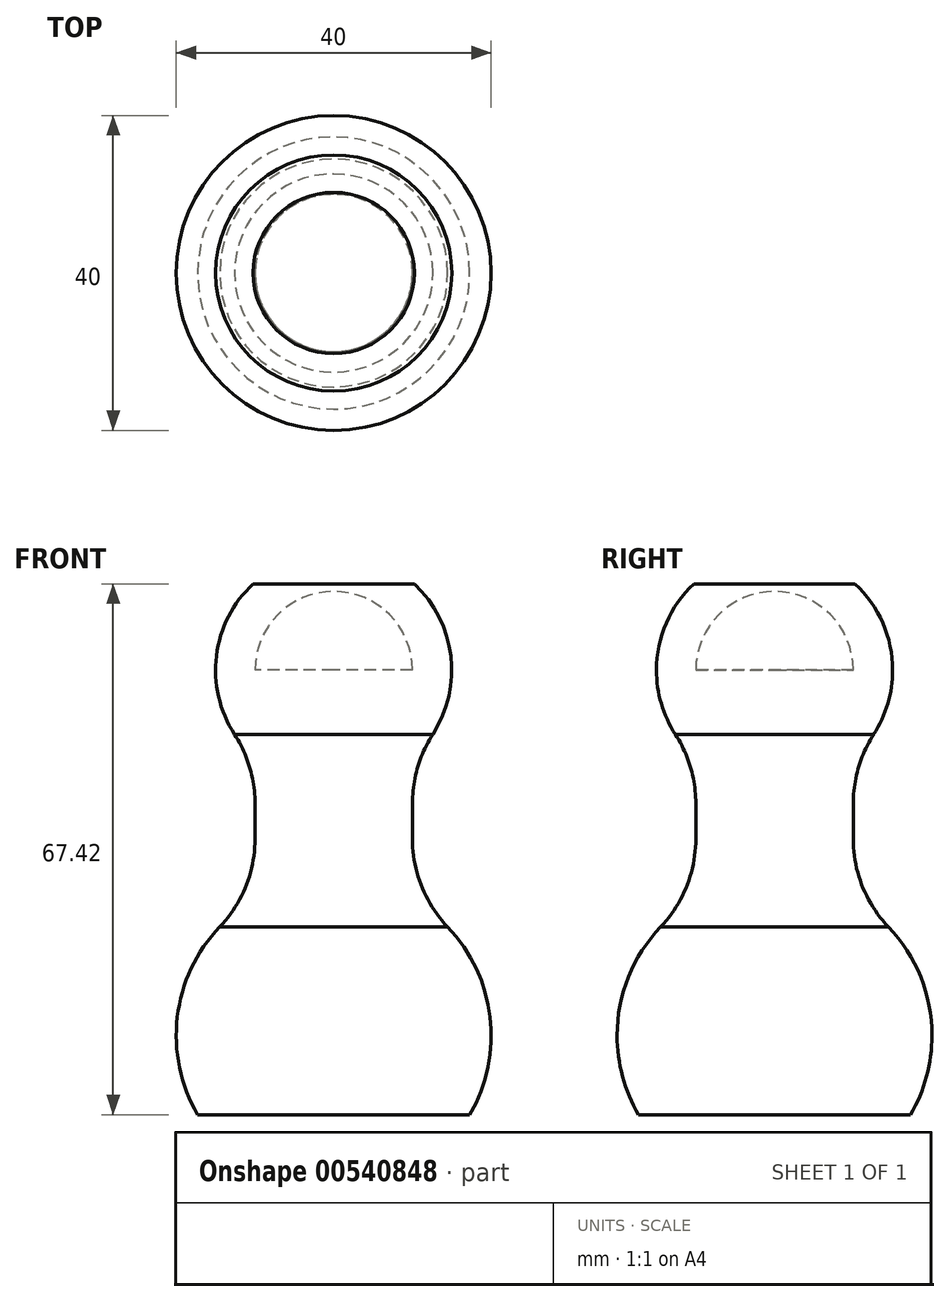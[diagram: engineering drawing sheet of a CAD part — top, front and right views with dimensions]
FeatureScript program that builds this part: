
annotation { "Feature Type Name" : "Feature", "Feature Type Description" : "" }
export const myFeature = defineFeature(function(context is Context, id is Id, definition is map)
    precondition{}
    {
        {
            var Q0;
            Q0=qCreatedBy(makeId("Top.planeOp"),FACE);
            var sketch = newSketch(context, id + "F0", { "sketchPlane" : qUnion([Q0])});
            skArc(sketch, "E0", {"start": v(0, 20) * mm, "mid": v(-20, 0) * mm, "end": v(0, -20) * mm});
            skLineSegment(sketch, "E1", {"start": v(0, 20) * mm, "end": v(0, -20) * mm});
            skSolve(sketch);
        }
        {
            var Q0;
            Q0=makeQuery(id+"F0.imprint","IMPRINT",FACE,{"disambiguationData":[TD([[makeQuery(id+"F0.imprint","IMPRINT",EDGE,{"derivedFrom":sQuery(id+"F0.wireOp",EDGE,"E0")}),1.0]])]});
            var Q1;
            Q1=sQuery(id+"F0.wireOp",EDGE,"E1");
            revolve(context, id + "F1", {"entities" : qUnion([Q0]), "axis" : qUnion([Q1]), "revolveType" : RevolveType.FULL});
        }
        {
            var Q0;
            Q0=qCreatedBy(makeId("Top.planeOp"),FACE);
            var sketch = newSketch(context, id + "F2", { "sketchPlane" : qUnion([Q0])});
            skCircle(sketch, "E2", {"center": v(0, 0) * mm, "radius": 10 * mm});
            skSolve(sketch);
        }
        {
            var Q0;
            Q0 = qSketchRegion(id + "F2", true);
            extrude(context, id + "F3", {"entities" : qUnion([Q0]), "operationType" : NewBodyOperationType.ADD, "depth" : 46.4 * mm, "offsetDistance" : 25 * mm});
        }
        {
            var Q0;
            Q0=makeQuery(id+"F3.opExtrude","CAP_FACE",FACE,{"disambiguationData":[OSD([sQuery(id+"F2.wireOp",EDGE,"E2")])],"isStart":false});
            var sketch = newSketch(context, id + "F4", { "sketchPlane" : qUnion([Q0])});
            skArc(sketch, "E3", {"start": v(0, 15) * mm, "mid": v(-15, 0) * mm, "end": v(0, -15) * mm});
            skLineSegment(sketch, "E4", {"start": v(0, 15) * mm, "end": v(0, -15) * mm});
            skSolve(sketch);
        }
        {
            var Q0;
            Q0=makeQuery(id+"F4.imprint","IMPRINT",FACE,{"disambiguationData":[TD([[makeQuery(id+"F4.imprint","IMPRINT",EDGE,{"derivedFrom":sQuery(id+"F4.wireOp",EDGE,"E3")}),1.0]])]});
            var Q1;
            Q1=sQuery(id+"F4.wireOp",EDGE,"E4");
            revolve(context, id + "F5", {"operationType" : NewBodyOperationType.ADD, "entities" : qUnion([Q0]), "axis" : qUnion([Q1]), "revolveType" : RevolveType.FULL});
        }
        {
            var Q0;
            Q0=makeQuery(id+"F5.boolean.opBoolean","INTERSECT",EDGE,{"derivedFrom":[makeQuery(id+"F3.opExtrude","SWEPT_FACE",FACE,{"disambiguationData":[OSD([sQuery(id+"F2.wireOp",EDGE,"E2")])]}),makeQuery(id+"F5.opRevolve","SWEPT_FACE",FACE,{"disambiguationData":[OSD([sQuery(id+"F4.wireOp",EDGE,"E3")])]})]});
            var Q1;
            Q1=makeQuery(id+"F3.boolean.opBoolean","INTERSECT",EDGE,{"derivedFrom":[makeQuery(id+"F1.opRevolve","SWEPT_FACE",FACE,{"disambiguationData":[OSD([sQuery(id+"F0.wireOp",EDGE,"E0")])]}),makeQuery(id+"F3.opExtrude","SWEPT_FACE",FACE,{"disambiguationData":[OSD([sQuery(id+"F2.wireOp",EDGE,"E2")])]})]});
            fillet(context, id + "F6", {"entities" : qUnion([Q0, Q1]), "radius" : 16.16 * mm, "tangentPropagation" : true, "allowEdgeOverflow" : false});
        }
        {
            var Q0;
            Q0=qCreatedBy(makeId("Front.planeOp"),FACE);
            var sketch = newSketch(context, id + "F7", { "sketchPlane" : qUnion([Q0])});
            skLineSegment(sketch, "E5.bottom", {"start": v(-35.85, 57.36) * mm, "end": v(40.38, 57.36) * mm});
            skLineSegment(sketch, "E5.top", {"start": v(-35.85, -10.06) * mm, "end": v(40.38, -10.06) * mm});
            skLineSegment(sketch, "E5.left", {"start": v(-35.85, 57.36) * mm, "end": v(-35.85, -10.06) * mm});
            skLineSegment(sketch, "E5.right", {"start": v(40.38, 57.36) * mm, "end": v(40.38, -10.06) * mm});
            skSolve(sketch);
        }
        {
            var Q0;
            Q0=makeQuery(id+"F7.imprint","IMPRINT",FACE,{"disambiguationData":[TD([[makeQuery(id+"F7.imprint","IMPRINT",EDGE,{"derivedFrom":sQuery(id+"F7.wireOp",EDGE,"E5.bottom")}),-1.0]])]});
            extrude(context, id + "F8", {"entities" : qUnion([Q0]), "operationType" : NewBodyOperationType.INTERSECT, "endBound" : BoundingType.SYMMETRIC, "depth" : 49.6 * mm, "offsetDistance" : 25 * mm});
        }
        {
            var Q0;
            Q0=qCreatedBy(makeId("Front.planeOp"),FACE);
            var sketch = newSketch(context, id + "F9", { "sketchPlane" : qUnion([Q0])});
            skLineSegment(sketch, "E6", {"start": v(-61.16, -61.97) * mm, "end": v(41.95, 42.49) * mm});
            skSolve(sketch);
        }
    });
